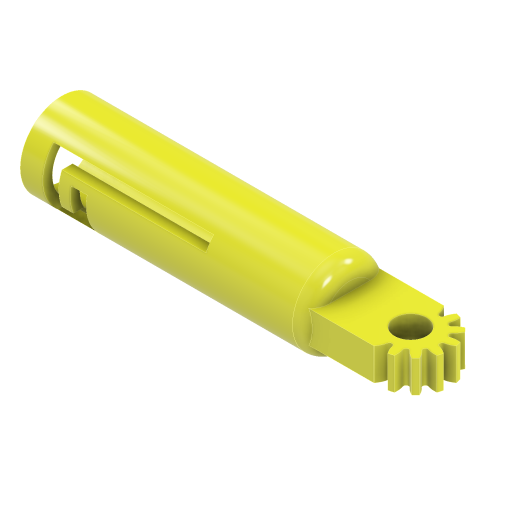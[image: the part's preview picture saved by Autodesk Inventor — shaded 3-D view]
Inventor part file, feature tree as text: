
AUTODESK INVENTOR PART (.ipt)
format: ipt  version: 2024 (Build 280153000, 153)  size: 427,008 bytes
history: native  units: mm
features: sketch x8, extrude x5, other x2, fillet x2, loft x1, shell x1, pattern_circular x1
ambient origin geometry x8: Origin, YZ Plane, XZ Plane, XY Plane, X Axis, Y Axis, Z Axis, Center Point
bodies: Solido1 (feature_tree)
feature tree (20):
  sketch  "Schizzo1"
  sketch  "Schizzo2"
  other  "Piano di lavoro1"
  loft  "Loft1"
  shell  "Svuotamento1"  Thickness=15.0mm
  other  "Piano di lavoro3"
  sketch  "Schizzo11"
  extrude  "Estrusione5"  Depth=26.0mm
  extrude  "Estrusione6"  Depth=26.0mm
  extrude  "Estrusione7"  Depth=25.0mm
  fillet  "Raccordo3"  Radius=17.0mm
  extrude  "Estrusione8"  Depth=10.0mm
  fillet  "Raccordo4"  Radius=5.0mm
  sketch  "Schizzo14"
  extrude  "Extrusion9"  Depth=12.5mm
  pattern_circular  "Circular Pattern1"  [2 undecoded]
  sketch  "Schizzo3"
  sketch  "Schizzo12"
  sketch  "Schizzo13"
  sketch  "Sketch15"  dims[d0=30.0mm d1=90.0mm d2=15.0mm d3=26.0mm d4=26.0mm d5=25.0mm d6=17.0mm d7=10.0mm d8=5.0mm d9=12.5mm d10=5.0mm d11=2.5mm d13=80.0mm d16=75.0mm d17=0.0mm d18=90.0deg d19=0.0mm d20=90.0deg d21=3.0mm d53=24.0mm d54=10.0mm d55=0.0mm d58=10.0mm d59=21.817424mm d60=31.4mm d61=0.0mm d64=21.817212mm d70=10.0mm d71=12.5mm d72=10.9085mm d73=25.0mm d74=0.0mm d75=18.9mm d76=100.0mm d77=5.0mm d79=28.0mm d80=50.0mm d83=5.0mm d84=5.0mm d85=7.797239mm d86=5.0mm d87=5.0mm d88=10.0mm d89=0.0mm d90=10.909mm d91=21.818mm d92=10.908712mm d93=10.908712mm d94=0.0mm d95=10.0mm d96=10.0mm d97=0.0mm d98=40.0mm d100=90.0deg d102=40.0mm d104=90.0deg d106=70.0mm d107=180.0deg d22=0.872665mm d23=0.5mm d24=0.872665mm d38=0.5mm d39=0.872665mm d40=0.5mm d41=0.872665mm]
note: 2 required parameter values undecoded (feature->parameter linkage not recoverable at this tier; creation-order binding heuristic only, values carry confidence <= 0.55)
